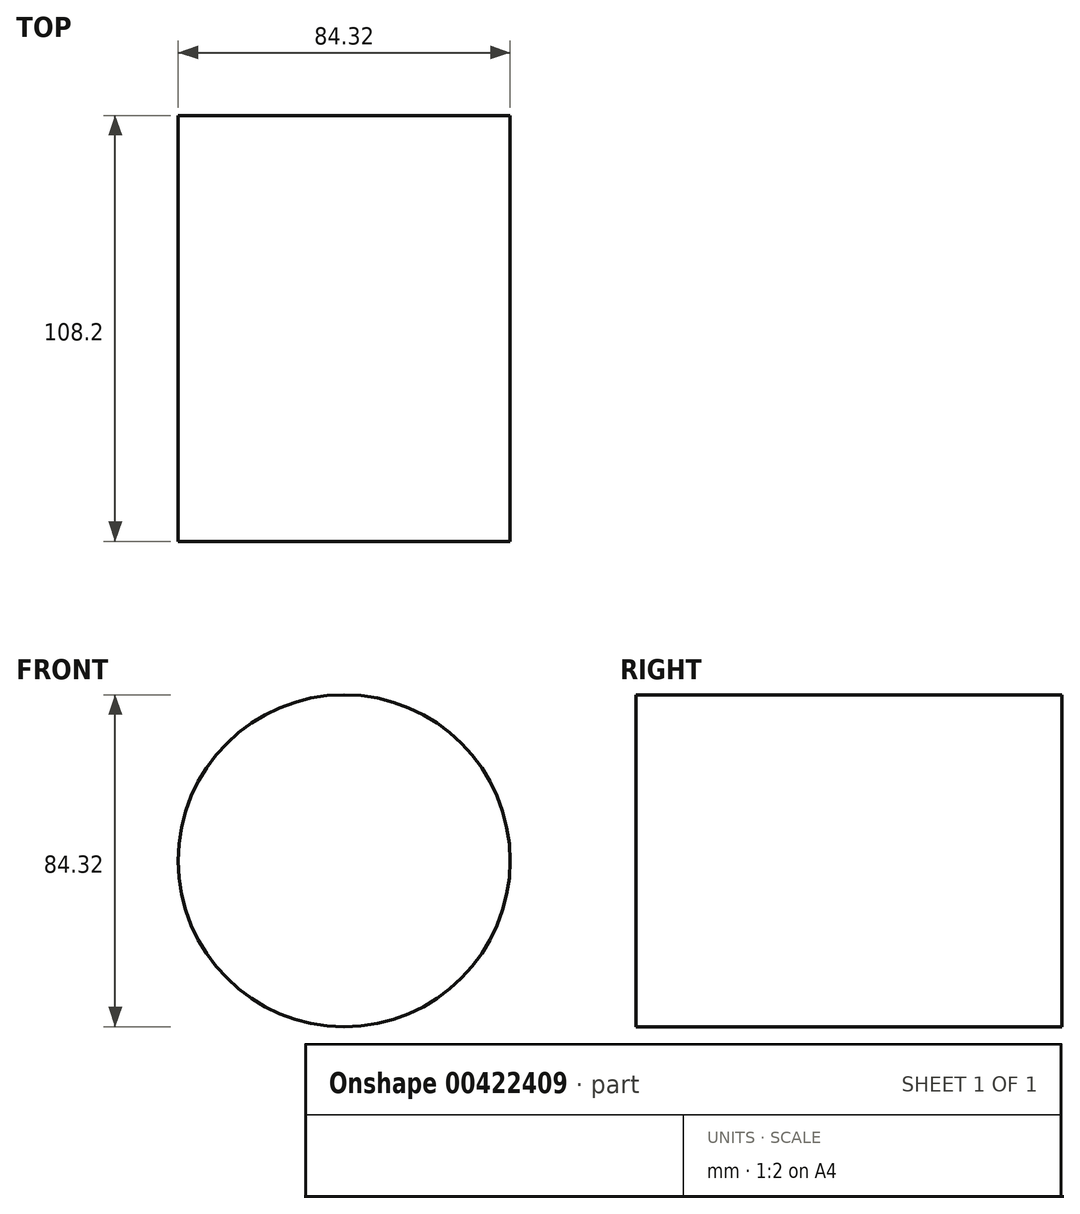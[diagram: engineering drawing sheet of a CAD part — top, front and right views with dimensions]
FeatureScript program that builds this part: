
annotation { "Feature Type Name" : "Feature", "Feature Type Description" : "" }
export const myFeature = defineFeature(function(context is Context, id is Id, definition is map)
    precondition{}
    {
        {
            var Q0;
            Q0=qCreatedBy(makeId("Front.planeOp"),FACE);
            var sketch = newSketch(context, id + "F0", { "sketchPlane" : qUnion([Q0])});
            skCircle(sketch, "E0", {"center": v(0, 0) * mm, "radius": 42.16 * mm});
            skSolve(sketch);
        }
        {
            var Q0;
            Q0=makeQuery(id+"F0.imprint","IMPRINT",FACE,{"disambiguationData":[TD([[makeQuery(id+"F0.imprint","IMPRINT",EDGE,{"derivedFrom":sQuery(id+"F0.wireOp",EDGE,"E0")}),1.0]])]});
            var sketch = newSketch(context, id + "F1", { "sketchPlane" : qUnion([Q0])});
            skSolve(sketch);
        }
        {
            var Q0;
            Q0=makeQuery(id+"F0.imprint","IMPRINT",FACE,{"disambiguationData":[TD([[makeQuery(id+"F0.imprint","IMPRINT",EDGE,{"derivedFrom":sQuery(id+"F0.wireOp",EDGE,"E0")}),1.0]])]});
            extrude(context, id + "F2", {"entities" : qUnion([Q0]), "depth" : 32 * mm});
        }
        {
            var Q0;
            Q0 = qSketchRegion(id + "FyJb46f58ALgxEp_0", true);
            var Q1;
            Q1=makeQuery(id+"F0.imprint","IMPRINT",FACE,{"disambiguationData":[TD([[makeQuery(id+"F0.imprint","IMPRINT",EDGE,{"derivedFrom":sQuery(id+"F0.wireOp",EDGE,"E0")}),1.0]])]});
            var Q2;
            Q2=makeQuery(id+"F1.imprint","IMPRINT",FACE,{"disambiguationData":[TD([[makeQuery(id+"F1.imprint","IMPRINT",EDGE,{"derivedFrom":makeQuery(id+"F0.imprint","IMPRINT",EDGE,{"derivedFrom":sQuery(id+"F0.wireOp",EDGE,"E0")})}),1.0]])]});
            var Q3;
            Q3=makeQuery(id+"F2.opExtrude","CAP_FACE",FACE,{"disambiguationData":[OSD([sQuery(id+"F0.wireOp",EDGE,"E0")])],"isStart":true});
            var Q4;
            Q4=makeQuery(id+"F2.opExtrude","CAP_FACE",FACE,{"disambiguationData":[OSD([sQuery(id+"F0.wireOp",EDGE,"E0")])],"isStart":false});
            extrude(context, id + "F3", {"entities" : qUnion([Q0, Q1, Q2, Q3, Q4]), "operationType" : NewBodyOperationType.ADD, "depth" : 25.4 * mm});
        }
        {
            var Q0;
            {var subQ0=sQuery(id+"F0.wireOp",EDGE,"E0");Q0=makeQuery(id+"F3.opExtrude","CAP_FACE",FACE,{"disambiguationData":[OSD([subQ0]),TDD([makeQuery(id+"F2.opExtrude","CAP_FACE",FACE,{"disambiguationData":[OSD([subQ0])],"isStart":false})])],"isStart":false});}
            var Q1;
            Q1=makeQuery(id+"F2.opExtrude","CAP_FACE",FACE,{"disambiguationData":[OSD([sQuery(id+"F0.wireOp",EDGE,"E0")])],"isStart":true});
            var Q2;
            Q2 = qSketchRegion(id + "FyJb46f58ALgxEp_0", true);
            var Q3;
            Q3=makeQuery(id+"F0.imprint","IMPRINT",FACE,{"disambiguationData":[TD([[makeQuery(id+"F0.imprint","IMPRINT",EDGE,{"derivedFrom":sQuery(id+"F0.wireOp",EDGE,"E0")}),1.0]])]});
            var Q4;
            Q4=makeQuery(id+"F1.imprint","IMPRINT",FACE,{"disambiguationData":[TD([[makeQuery(id+"F1.imprint","IMPRINT",EDGE,{"derivedFrom":makeQuery(id+"F0.imprint","IMPRINT",EDGE,{"derivedFrom":sQuery(id+"F0.wireOp",EDGE,"E0")})}),1.0]])]});
            extrude(context, id + "F4", {"entities" : qUnion([Q0, Q1, Q2, Q3, Q4]), "operationType" : NewBodyOperationType.ADD, "depth" : 25.4 * mm});
        }
        {
            var Q0;
            {var subQ0=sQuery(id+"F0.wireOp",EDGE,"E0");Q0=makeQuery(id+"F4.opExtrude","CAP_FACE",FACE,{"disambiguationData":[OSD([subQ0]),TDD([makeQuery(id+"F3.opExtrude","CAP_FACE",FACE,{"disambiguationData":[OSD([subQ0]),TDD([makeQuery(id+"F2.opExtrude","CAP_FACE",FACE,{"disambiguationData":[OSD([subQ0])],"isStart":false})])],"isStart":false})])],"isStart":false});}
            var Q1;
            Q1=makeQuery(id+"F1.imprint","IMPRINT",FACE,{"disambiguationData":[TD([[makeQuery(id+"F1.imprint","IMPRINT",EDGE,{"derivedFrom":makeQuery(id+"F0.imprint","IMPRINT",EDGE,{"derivedFrom":sQuery(id+"F0.wireOp",EDGE,"E0")})}),1.0]])]});
            var Q2;
            Q2=makeQuery(id+"F2.opExtrude","CAP_FACE",FACE,{"disambiguationData":[OSD([sQuery(id+"F0.wireOp",EDGE,"E0")])],"isStart":true});
            var Q3;
            Q3=makeQuery(id+"F0.imprint","IMPRINT",FACE,{"disambiguationData":[TD([[makeQuery(id+"F0.imprint","IMPRINT",EDGE,{"derivedFrom":sQuery(id+"F0.wireOp",EDGE,"E0")}),1.0]])]});
            extrude(context, id + "F5", {"entities" : qUnion([Q0, Q1, Q2, Q3]), "operationType" : NewBodyOperationType.ADD, "depth" : 25.4 * mm});
        }
    });
